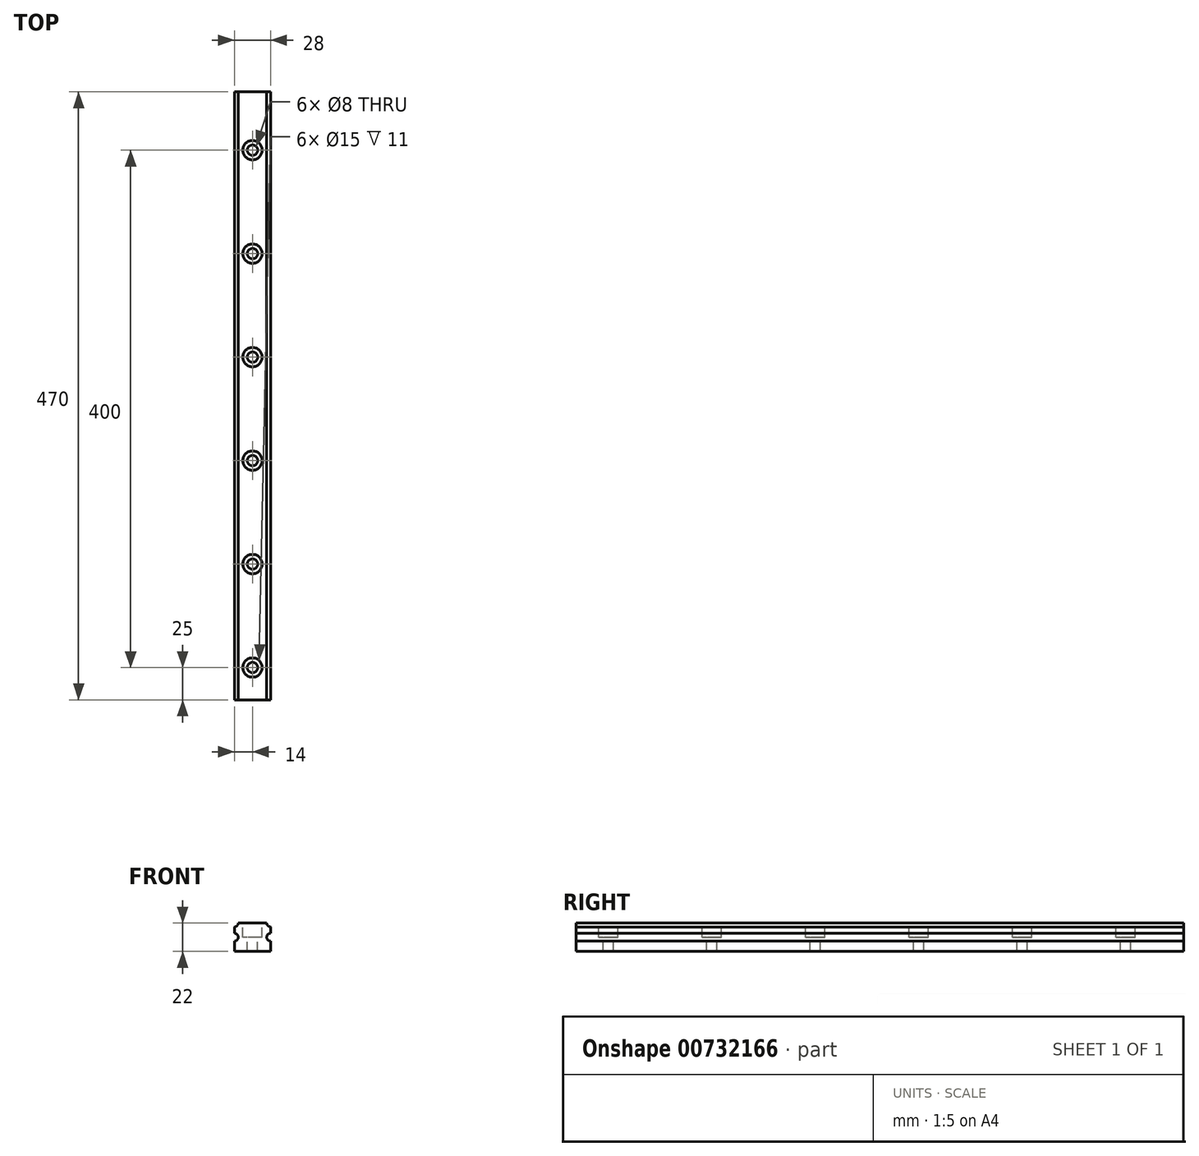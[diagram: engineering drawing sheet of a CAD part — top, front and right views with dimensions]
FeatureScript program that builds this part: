
annotation { "Feature Type Name" : "Feature", "Feature Type Description" : "" }
export const myFeature = defineFeature(function(context is Context, id is Id, definition is map)
    precondition{}
    {
        {
            var Q0;
            Q0=qCreatedBy(makeId("Front.planeOp"),FACE);
            var sketch = newSketch(context, id + "F0", { "sketchPlane" : qUnion([Q0])});
            skLineSegment(sketch, "E0", {"start": v(0, 0) * mm, "end": v(0, 8) * mm});
            skLineSegment(sketch, "E1", {"start": v(3, 22) * mm, "end": v(25, 22) * mm});
            skLineSegment(sketch, "E2", {"start": v(28, 19) * mm, "end": v(28, 14) * mm});
            skLineSegment(sketch, "E3", {"start": v(28, 0) * mm, "end": v(0, 0) * mm});
            skArc(sketch, "E4", {"start": v(0, 8) * mm, "mid": v(3, 11) * mm, "end": v(0, 14) * mm});
            skArc(sketch, "E5", {"start": v(28, 14) * mm, "mid": v(25, 11) * mm, "end": v(28, 8) * mm});
            skLineSegment(sketch, "E6.trimOffspring", {"start": v(28, 8) * mm, "end": v(28, 0) * mm});
            skLineSegment(sketch, "E7.trimOffspring", {"start": v(0, 14) * mm, "end": v(0, 19) * mm});
            skArc(sketch, "E8", {"start": v(0, 19) * mm, "mid": v(2.12, 19.88) * mm, "end": v(3, 22) * mm});
            skArc(sketch, "E9", {"start": v(25, 22) * mm, "mid": v(25.88, 19.88) * mm, "end": v(28, 19) * mm});
            skSolve(sketch);
        }
        {
            var Q0;
            Q0=makeQuery(id+"F0.imprint","IMPRINT",FACE,{"disambiguationData":[TD([[makeQuery(id+"F0.imprint","IMPRINT",EDGE,{"derivedFrom":sQuery(id+"F0.wireOp",EDGE,"E0")}),-1.0]])]});
            extrude(context, id + "F1", {"entities" : qUnion([Q0]), "depth" : 470 * mm});
        }
        {
            var Q0;
            Q0=makeQuery(id+"F1.opExtrude","SWEPT_FACE",FACE,{"disambiguationData":[OSD([sQuery(id+"F0.wireOp",EDGE,"E1")])]});
            var sketch = newSketch(context, id + "F2", { "sketchPlane" : qUnion([Q0])});
            skCircle(sketch, "E10", {"center": v(14, -45) * mm, "radius": 4 * mm});
            skCircle(sketch, "E11", {"center": v(14, -125) * mm, "radius": 4 * mm});
            skCircle(sketch, "E12", {"center": v(14, -205) * mm, "radius": 4 * mm});
            skCircle(sketch, "E13", {"center": v(14, -285) * mm, "radius": 4 * mm});
            skCircle(sketch, "E14", {"center": v(14, -365) * mm, "radius": 4 * mm});
            skCircle(sketch, "E15", {"center": v(14, -445) * mm, "radius": 4 * mm});
            skSolve(sketch);
        }
        {
            var Q0;
            Q0=qSketchRegion(id+"F2",true);
            extrude(context, id + "F3", {"entities" : qUnion([Q0]), "operationType" : NewBodyOperationType.REMOVE, "oppositeDirection" : true, "depth" : 25 * mm});
        }
        {
            var Q0;
            Q0=makeQuery(id+"F1.opExtrude","SWEPT_FACE",FACE,{"disambiguationData":[OSD([sQuery(id+"F0.wireOp",EDGE,"E1")])]});
            var sketch = newSketch(context, id + "F4", { "sketchPlane" : qUnion([Q0])});
            skCircle(sketch, "E16", {"center": v(14, -205) * mm, "radius": 7.5 * mm});
            skCircle(sketch, "E17", {"center": v(14, -125) * mm, "radius": 7.5 * mm});
            skCircle(sketch, "E18", {"center": v(14, -45) * mm, "radius": 7.5 * mm});
            skCircle(sketch, "E19", {"center": v(14, -285) * mm, "radius": 7.5 * mm});
            skCircle(sketch, "E20", {"center": v(14, -365) * mm, "radius": 7.5 * mm});
            skCircle(sketch, "E21", {"center": v(14, -445) * mm, "radius": 7.5 * mm});
            skSolve(sketch);
        }
        {
            var Q0;
            Q0=qSketchRegion(id+"F4",true);
            extrude(context, id + "F5", {"entities" : qUnion([Q0]), "operationType" : NewBodyOperationType.REMOVE, "oppositeDirection" : true, "depth" : 11 * mm});
        }
    });
